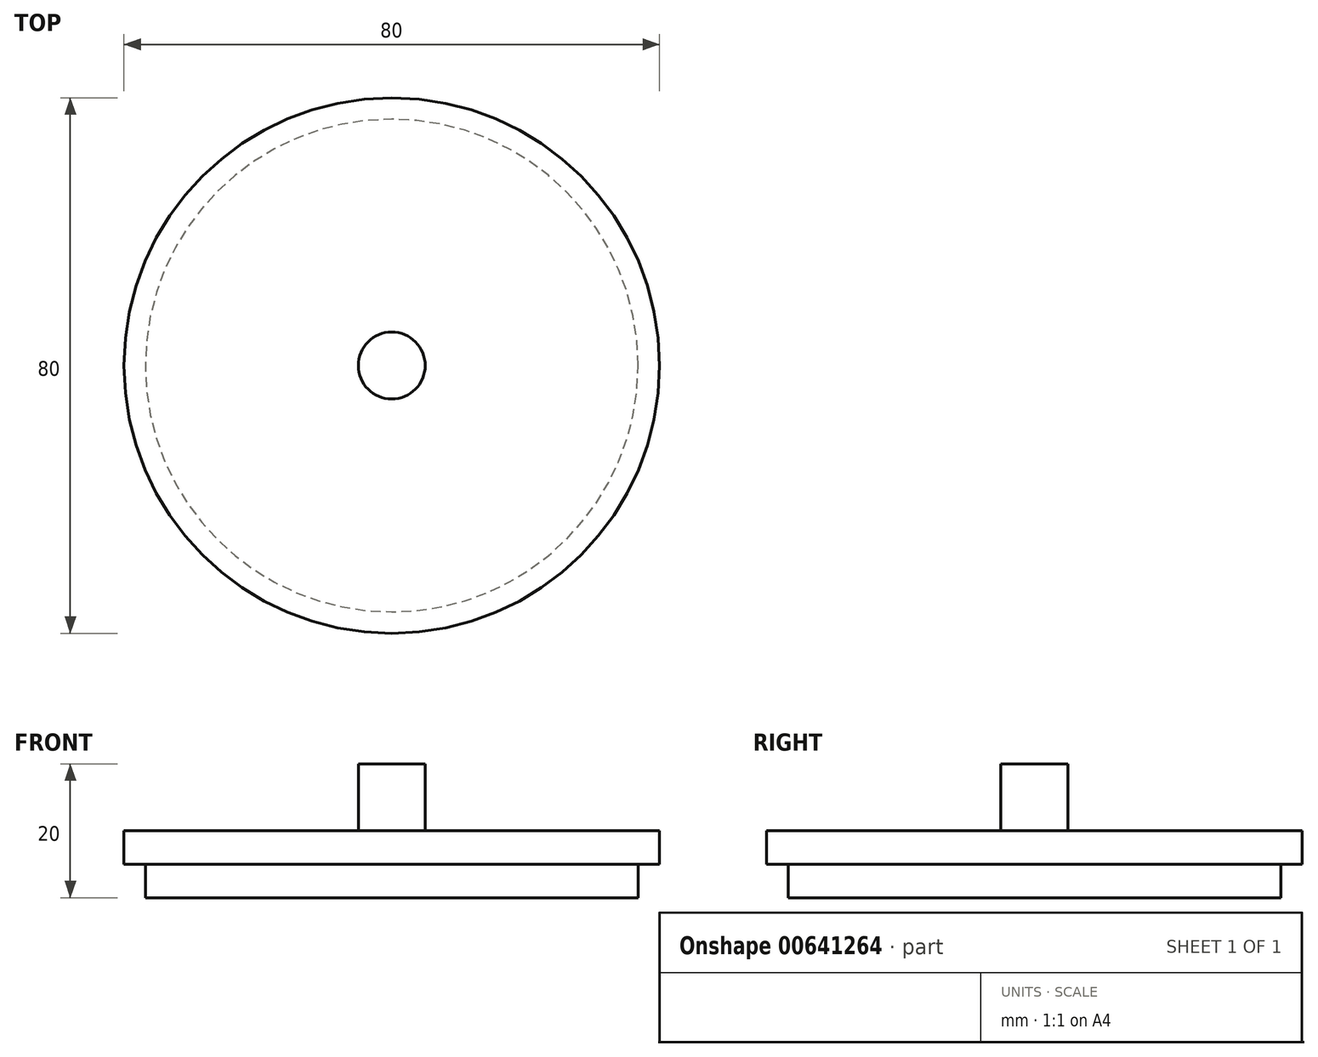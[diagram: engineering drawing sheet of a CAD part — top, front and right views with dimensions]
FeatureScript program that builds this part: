
annotation { "Feature Type Name" : "Feature", "Feature Type Description" : "" }
export const myFeature = defineFeature(function(context is Context, id is Id, definition is map)
    precondition{}
    {
        {
            var Q0;
            Q0=qCreatedBy(makeId("Front.planeOp"),FACE);
            var sketch = newSketch(context, id + "F0", { "sketchPlane" : qUnion([Q0])});
            skLineSegment(sketch, "E0", {"start": v(0, 0) * mm, "end": v(-36.8, 0) * mm});
            skLineSegment(sketch, "E1", {"start": v(-36.8, 0) * mm, "end": v(-36.8, 5) * mm});
            skLineSegment(sketch, "E2", {"start": v(-36.8, 5) * mm, "end": v(-40, 5) * mm});
            skLineSegment(sketch, "E3", {"start": v(-40, 5) * mm, "end": v(-40, 10) * mm});
            skLineSegment(sketch, "E4", {"start": v(-40, 10) * mm, "end": v(-5, 10) * mm});
            skLineSegment(sketch, "E5", {"start": v(-5, 10) * mm, "end": v(-5, 20) * mm});
            skLineSegment(sketch, "E6", {"start": v(-5, 20) * mm, "end": v(0, 20) * mm});
            skLineSegment(sketch, "E7", {"start": v(0, 20) * mm, "end": v(0, 0) * mm});
            skSolve(sketch);
        }
        {
            var Q0;
            Q0=makeQuery(id+"F0.imprint","IMPRINT",FACE,{"disambiguationData":[TD([[makeQuery(id+"F0.imprint","IMPRINT",EDGE,{"derivedFrom":sQuery(id+"F0.wireOp",EDGE,"E0")}),-1.0]])]});
            var Q1;
            Q1=sQuery(id+"F0.wireOp",EDGE,"E7");
            revolve(context, id + "F1", {"entities" : qUnion([Q0]), "axis" : qUnion([Q1]), "revolveType" : RevolveType.FULL});
        }
    });
